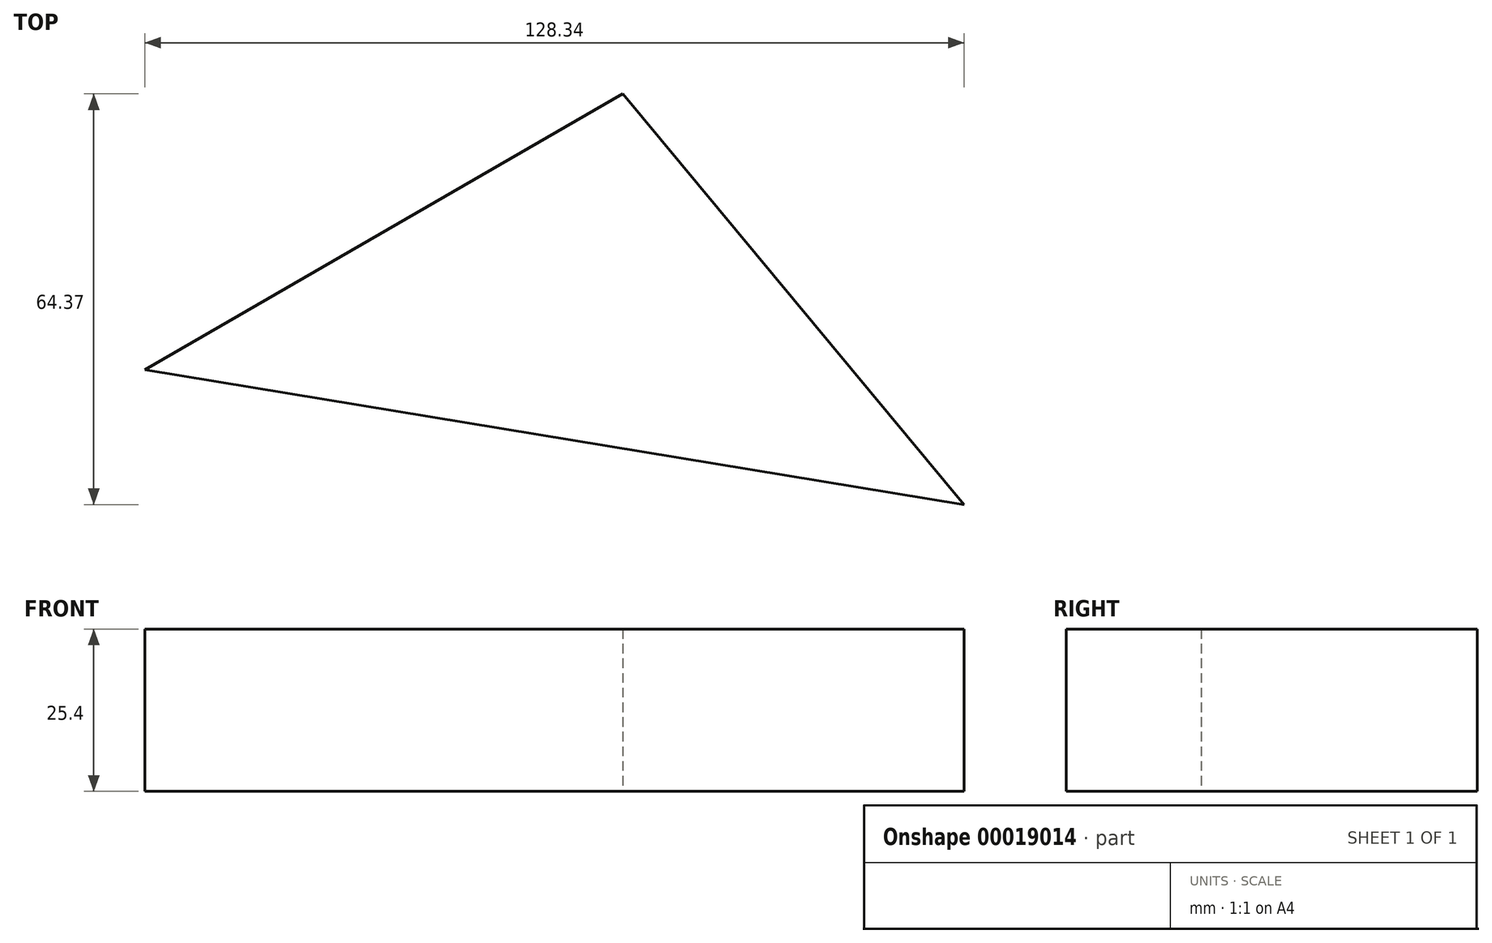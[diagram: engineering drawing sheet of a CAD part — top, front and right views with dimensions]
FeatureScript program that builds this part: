
annotation { "Feature Type Name" : "Feature", "Feature Type Description" : "" }
export const myFeature = defineFeature(function(context is Context, id is Id, definition is map)
    precondition{}
    {
        {
            var Q0;
            Q0=qCreatedBy(makeId("Top.planeOp"),FACE);
            var sketch = newSketch(context, id + "F0", { "sketchPlane" : qUnion([Q0])});
            skLineSegment(sketch, "E0", {"start": v(-80.61, -61.5) * mm, "end": v(-5.77, -18.3) * mm});
            skLineSegment(sketch, "E1", {"start": v(-5.77, -18.3) * mm, "end": v(47.73, -82.67) * mm});
            skLineSegment(sketch, "E2", {"start": v(47.73, -82.67) * mm, "end": v(-80.61, -61.5) * mm});
            skSolve(sketch);
        }
        {
            var Q0;
            Q0=makeQuery(id+"F0.imprint","IMPRINT",FACE,{"disambiguationData":[TD([[makeQuery(id+"F0.imprint","IMPRINT",EDGE,{"derivedFrom":sQuery(id+"F0.wireOp",EDGE,"E0")}),-1.0]])]});
            extrude(context, id + "F1", {"entities" : qUnion([Q0]), "depth" : 25.4 * mm});
        }
    });
